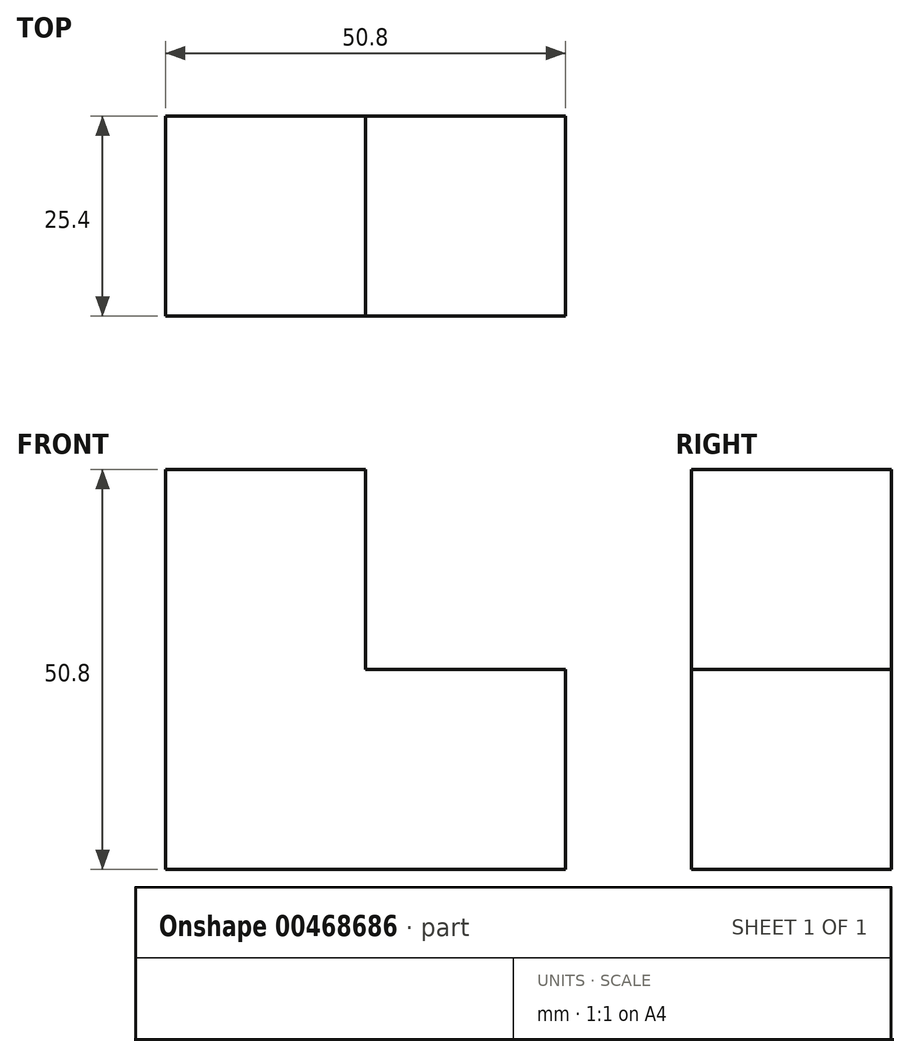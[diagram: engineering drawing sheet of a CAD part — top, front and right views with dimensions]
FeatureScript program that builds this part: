
annotation { "Feature Type Name" : "Feature", "Feature Type Description" : "" }
export const myFeature = defineFeature(function(context is Context, id is Id, definition is map)
    precondition{}
    {
        {
            var Q0;
            Q0=qCreatedBy(makeId("Front.planeOp"),FACE);
            var sketch = newSketch(context, id + "F0", { "sketchPlane" : qUnion([Q0])});
            skLineSegment(sketch, "E0.bottom", {"start": v(-44.53, 55.61) * mm, "end": v(-19.13, 55.61) * mm});
            skLineSegment(sketch, "E0.top", {"start": v(-44.53, 4.81) * mm, "end": v(-19.13, 4.81) * mm});
            skLineSegment(sketch, "E0.left", {"start": v(-44.53, 55.61) * mm, "end": v(-44.53, 4.81) * mm});
            skLineSegment(sketch, "E1.bottom", {"start": v(-19.13, 4.81) * mm, "end": v(6.27, 4.81) * mm});
            skLineSegment(sketch, "E1.top", {"start": v(-19.13, 30.21) * mm, "end": v(6.27, 30.21) * mm});
            skLineSegment(sketch, "E1.right", {"start": v(6.27, 4.81) * mm, "end": v(6.27, 30.21) * mm});
            skLineSegment(sketch, "E2", {"start": v(-19.13, 30.21) * mm, "end": v(-19.13, 55.61) * mm});
            skSolve(sketch);
        }
        {
            var Q0;
            Q0=makeQuery(id+"F0.imprint","IMPRINT",FACE,{"disambiguationData":[TD([[makeQuery(id+"F0.imprint","IMPRINT",EDGE,{"derivedFrom":sQuery(id+"F0.wireOp",EDGE,"E0.bottom")}),-1.0]])]});
            extrude(context, id + "F1", {"entities" : qUnion([Q0]), "depth" : 25.4 * mm});
        }
    });
